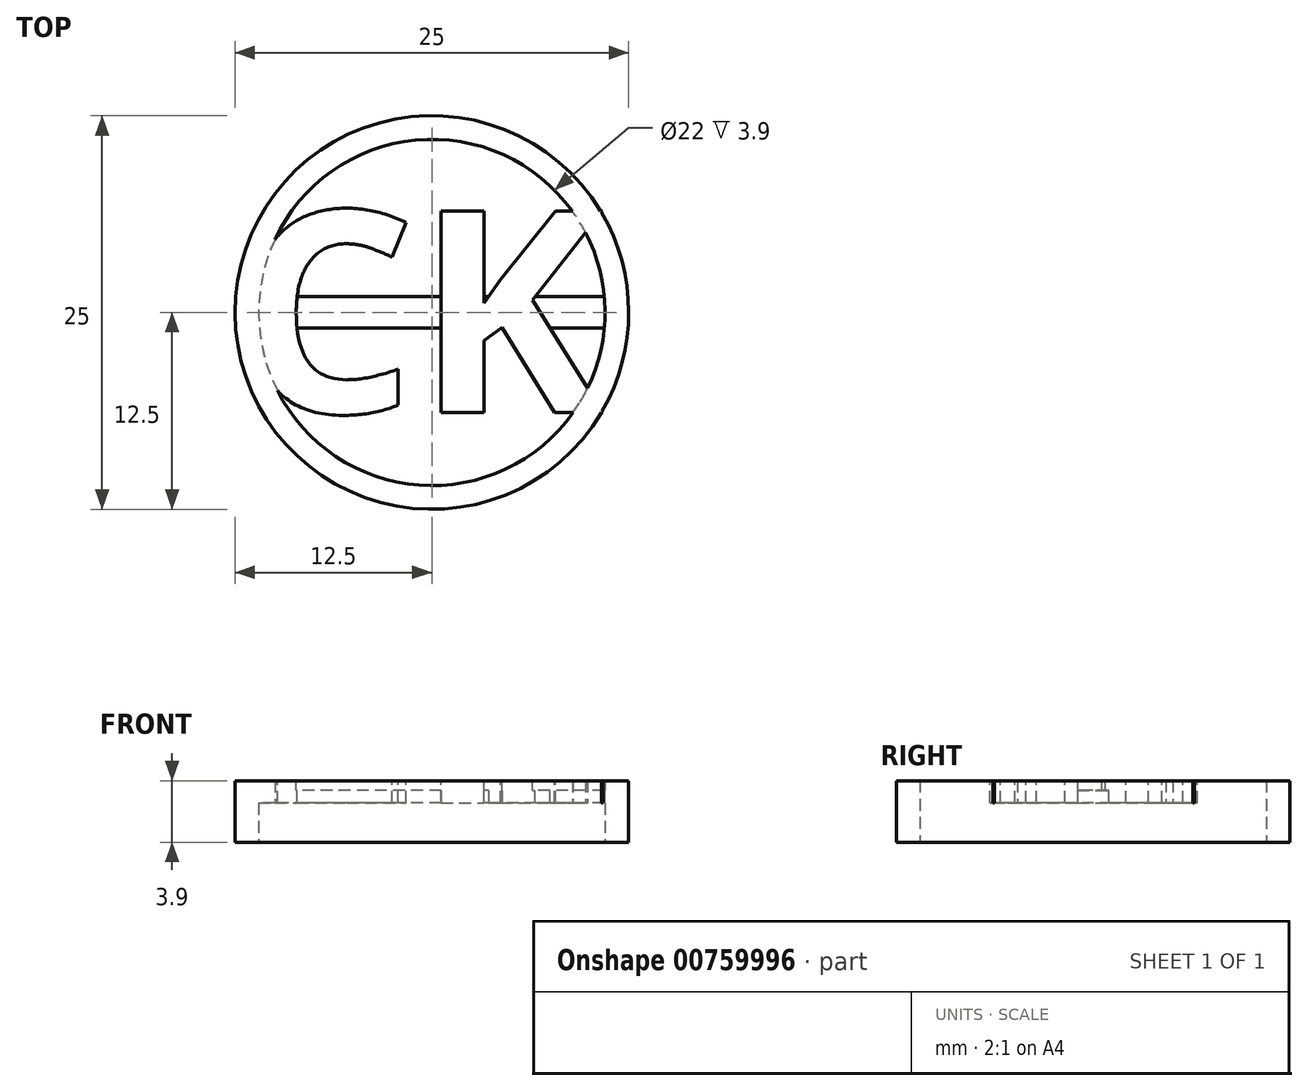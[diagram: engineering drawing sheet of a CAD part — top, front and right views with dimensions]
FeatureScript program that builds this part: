
annotation { "Feature Type Name" : "Feature", "Feature Type Description" : "" }
export const myFeature = defineFeature(function(context is Context, id is Id, definition is map)
    precondition{}
    {
        {
            var Q0;
            Q0=qCreatedBy(makeId("Top.planeOp"),FACE);
            var sketch = newSketch(context, id + "F0", { "sketchPlane" : qUnion([Q0])});
            skCircle(sketch, "E0", {"center": v(0, 0) * mm, "radius": 11 * mm});
            skCircle(sketch, "E1.0", {"center": v(0, 0) * mm, "radius": 12.5 * mm});
            skSolve(sketch);
        }
        {
            var Q0;
            Q0 = qSketchRegion(id + "F0", true);
            extrude(context, id + "F1", {"entities" : qUnion([Q0]), "depth" : 3.9 * mm, "offsetDistance" : 25 * mm});
        }
        {
            var Q0;
            Q0=qCreatedBy(makeId("Top.planeOp"),FACE);
            cPlane(context, id + "F2", {"entities" : qUnion([Q0]), "cplaneType" : CPlaneType.OFFSET, "offset" : 3.9 * mm, "width" : 150 * mm, "height" : 150 * mm});
        }
        {
            var Q0;
            Q0=qCreatedBy(id+"F2.planeOp",FACE);
            var sketch = newSketch(context, id + "F3", { "sketchPlane" : qUnion([Q0])});
            skText(sketch, "E2", { "text": "CK", "fontName": "NotoSans-Bold.ttf"});
            const initialGuessF3  = {"E2": [-0.01245, -0.00636, 1, 0, 0.01291]};
            skSetInitialGuess(sketch, initialGuessF3);
            skSolve(sketch);
        }
        {
            var Q0;
            Q0 = qSketchRegion(id + "F3", true);
            extrude(context, id + "F4", {"entities" : qUnion([Q0]), "operationType" : NewBodyOperationType.ADD, "oppositeDirection" : true, "depth" : 1.4 * mm, "offsetDistance" : 25 * mm});
        }
        {
            var Q0;
            Q0=qCreatedBy(makeId("Top.planeOp"),FACE);
            cPlane(context, id + "F5", {"entities" : qUnion([Q0]), "cplaneType" : CPlaneType.OFFSET, "offset" : 2.5 * mm, "width" : 150 * mm, "height" : 150 * mm});
        }
        {
            var Q0;
            Q0=qCreatedBy(id+"F5.planeOp",FACE);
            var sketch = newSketch(context, id + "F6", { "sketchPlane" : qUnion([Q0])});
            skLineSegment(sketch, "E3", {"start": v(0, 0) * mm, "end": v(0, 1) * mm});
            skLineSegment(sketch, "E4", {"start": v(0, 0) * mm, "end": v(1.54, 0) * mm});
            skLineSegment(sketch, "E5.MirrorCS", {"start": v(0, 0) * mm, "end": v(0, -1) * mm});
            skLineSegment(sketch, "E6", {"start": v(0, -1) * mm, "end": v(-9.57, -1) * mm});
            skLineSegment(sketch, "E7", {"start": v(0, -1) * mm, "end": v(11.2, -1) * mm});
            skLineSegment(sketch, "E8.bottom", {"start": v(0, 1) * mm, "end": v(11.2, 1) * mm});
            skLineSegment(sketch, "E8.left", {"start": v(0, 1) * mm, "end": v(0, -1) * mm});
            skLineSegment(sketch, "E8.right", {"start": v(11.2, 1) * mm, "end": v(11.2, -1) * mm});
            skLineSegment(sketch, "E9.bottom", {"start": v(0, 1) * mm, "end": v(-9.57, 1) * mm});
            skLineSegment(sketch, "E9.right", {"start": v(-9.57, 1) * mm, "end": v(-9.57, -1) * mm});
            skSolve(sketch);
        }
        {
            var Q0;
            Q0 = qSketchRegion(id + "F6", true);
            extrude(context, id + "F7", {"entities" : qUnion([Q0]), "operationType" : NewBodyOperationType.ADD, "depth" : .8 * mm, "offsetDistance" : 25 * mm});
        }
    });
